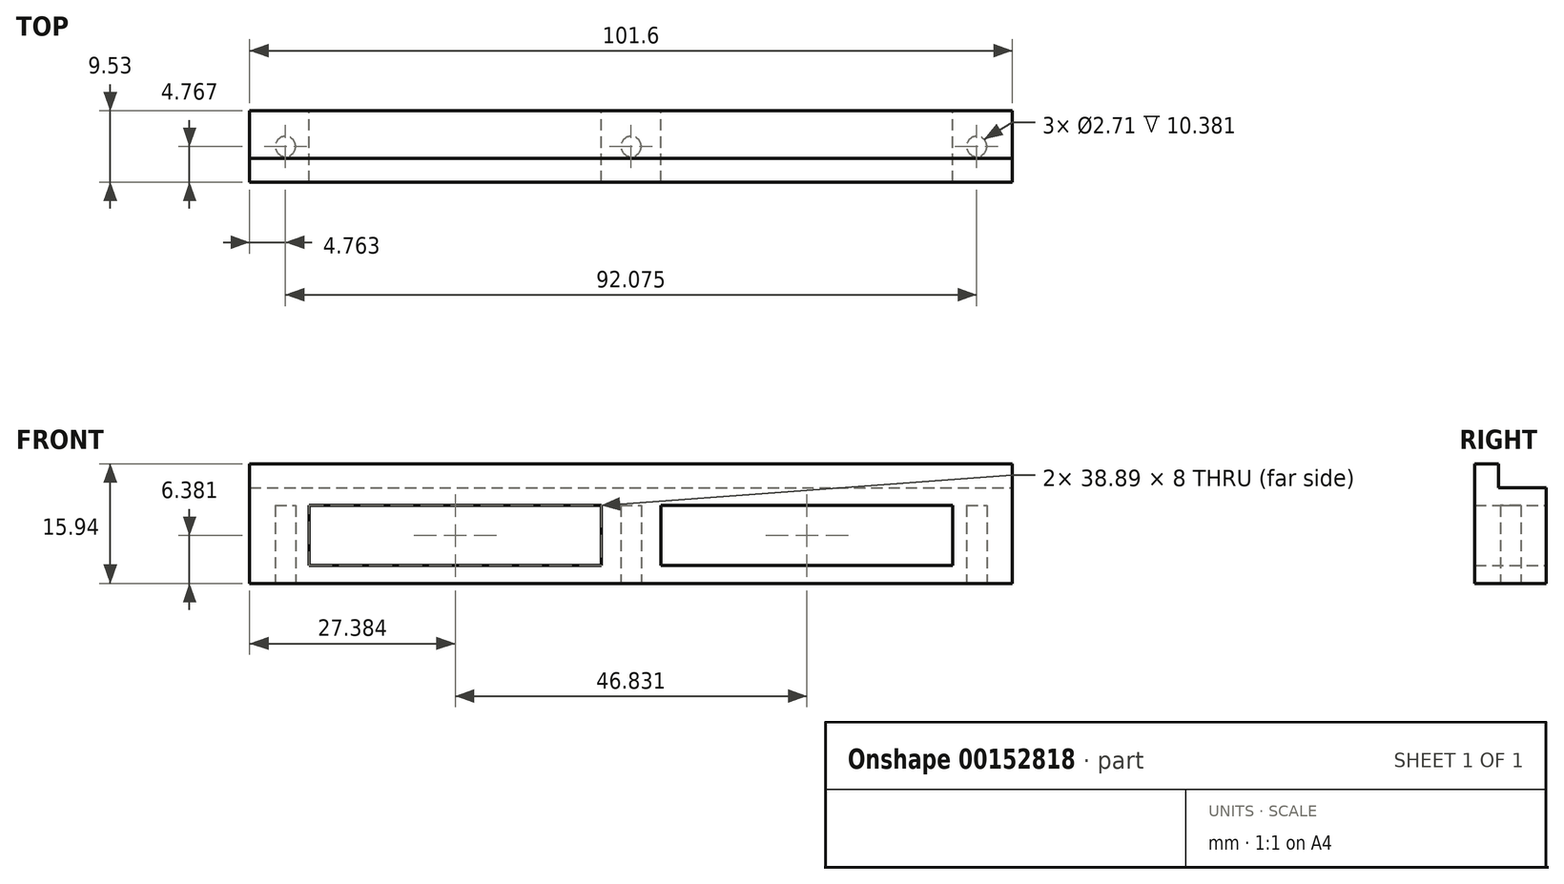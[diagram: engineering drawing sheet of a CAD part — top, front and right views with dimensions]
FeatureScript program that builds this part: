
annotation { "Feature Type Name" : "Feature", "Feature Type Description" : "" }
export const myFeature = defineFeature(function(context is Context, id is Id, definition is map)
    precondition{}
    {
        {
            var Q0;
            Q0=qCreatedBy(makeId("Top.planeOp"),FACE);
            var sketch = newSketch(context, id + "F0", { "sketchPlane" : qUnion([Q0])});
            skLineSegment(sketch, "E0.bottom", {"start": v(0, 0) * mm, "end": v(101.6, 0) * mm});
            skLineSegment(sketch, "E0.top", {"start": v(0, -9.53) * mm, "end": v(101.6, -9.53) * mm});
            skLineSegment(sketch, "E0.left", {"start": v(0, 0) * mm, "end": v(0, -9.53) * mm});
            skLineSegment(sketch, "E0.right", {"start": v(101.6, 0) * mm, "end": v(101.6, -9.52) * mm});
            skSolve(sketch);
        }
        {
            var Q0;
            Q0 = qSketchRegion(id + "F0", true);
            extrude(context, id + "F1", {"entities" : qUnion([Q0]), "depth" : 12.76 * mm});
        }
        {
            var Q0;
            Q0=makeQuery(id+"F1.opExtrude","CAP_FACE",FACE,{"disambiguationData":[OSD([sQuery(id+"F0.wireOp",EDGE,"E0.bottom"),sQuery(id+"F0.wireOp",EDGE,"E0.top"),sQuery(id+"F0.wireOp",EDGE,"E0.left"),sQuery(id+"F0.wireOp",EDGE,"E0.right")])],"isStart":false});
            var sketch = newSketch(context, id + "F2", { "sketchPlane" : qUnion([Q0])});
            skLineSegment(sketch, "E1.bottom", {"start": v(0, -9.53) * mm, "end": v(101.6, -9.53) * mm});
            skLineSegment(sketch, "E1.top", {"start": v(0, -6.35) * mm, "end": v(101.6, -6.35) * mm});
            skLineSegment(sketch, "E1.left", {"start": v(0, -9.53) * mm, "end": v(0, -6.35) * mm});
            skLineSegment(sketch, "E1.right", {"start": v(101.6, -9.53) * mm, "end": v(101.6, -6.35) * mm});
            skSolve(sketch);
        }
        {
            var Q0;
            Q0 = qSketchRegion(id + "F2", true);
            extrude(context, id + "F3", {"entities" : qUnion([Q0]), "operationType" : NewBodyOperationType.ADD, "depth" : 3.17 * mm});
        }
        {
            var Q0;
            Q0=makeQuery(id+"F1.opExtrude","SWEPT_FACE",FACE,{"disambiguationData":[OSD([sQuery(id+"F0.wireOp",EDGE,"E0.bottom")])]});
            var sketch = newSketch(context, id + "F4", { "sketchPlane" : qUnion([Q0])});
            skLineSegment(sketch, "E2.bottom", {"start": v(-93.66, 10.38) * mm, "end": v(-54.77, 10.38) * mm});
            skLineSegment(sketch, "E2.top", {"start": v(-93.66, 2.38) * mm, "end": v(-54.77, 2.38) * mm});
            skLineSegment(sketch, "E2.left", {"start": v(-93.66, 10.38) * mm, "end": v(-93.66, 2.38) * mm});
            skLineSegment(sketch, "E2.right", {"start": v(-54.77, 10.38) * mm, "end": v(-54.77, 2.38) * mm});
            skLineSegment(sketch, "E3.bottom", {"start": v(-46.83, 10.38) * mm, "end": v(-7.94, 10.38) * mm});
            skLineSegment(sketch, "E3.top", {"start": v(-46.83, 2.38) * mm, "end": v(-7.94, 2.38) * mm});
            skLineSegment(sketch, "E3.left", {"start": v(-46.83, 10.38) * mm, "end": v(-46.83, 2.38) * mm});
            skLineSegment(sketch, "E3.right", {"start": v(-7.94, 10.38) * mm, "end": v(-7.94, 2.38) * mm});
            skLineSegment(sketch, "E4", {"start": v(0, 6.38) * mm, "end": v(-7.94, 6.38) * mm, "construction": true});
            skLineSegment(sketch, "E5", {"start": v(-27.38, 2.38) * mm, "end": v(-27.38, 0) * mm, "construction": true});
            skLineSegment(sketch, "E6", {"start": v(-46.83, 6.38) * mm, "end": v(-54.77, 6.38) * mm, "construction": true});
            skLineSegment(sketch, "E7", {"start": v(-93.66, 6.38) * mm, "end": v(-101.6, 6.38) * mm, "construction": true});
            skSolve(sketch);
        }
        {
            var Q0;
            Q0 = qSketchRegion(id + "F4", true);
            var Q1;
            Q1=makeQuery(id+"F3.boolean.opBoolean","MERGE",FACE,{"derivedFrom":[makeQuery(id+"F1.opExtrude","SWEPT_FACE",FACE,{"disambiguationData":[OSD([sQuery(id+"F0.wireOp",EDGE,"E0.top")])]}),makeQuery(id+"F3.opExtrude","SWEPT_FACE",FACE,{"disambiguationData":[OSD([sQuery(id+"F2.wireOp",EDGE,"E1.bottom")])]})]});
            extrude(context, id + "F5", {"entities" : qUnion([Q0]), "operationType" : NewBodyOperationType.REMOVE, "endBound" : BoundingType.UP_TO_SURFACE, "oppositeDirection" : true, "endBoundEntityFace" : qUnion([Q1]), "depth" : 25.4 * mm});
        }
        {
            var Q0;
            Q0=makeQuery(id+"F1.opExtrude","CAP_FACE",FACE,{"disambiguationData":[OSD([sQuery(id+"F0.wireOp",EDGE,"E0.bottom"),sQuery(id+"F0.wireOp",EDGE,"E0.top"),sQuery(id+"F0.wireOp",EDGE,"E0.left"),sQuery(id+"F0.wireOp",EDGE,"E0.right")])],"isStart":true});
            var sketch = newSketch(context, id + "F6", { "sketchPlane" : qUnion([Q0])});
            skLineSegment(sketch, "E8.bottom", {"start": v(101.6, 4.76) * mm, "end": v(96.84, 4.76) * mm, "construction": true});
            skLineSegment(sketch, "E8.top", {"start": v(101.6, 9.53) * mm, "end": v(96.84, 9.53) * mm, "construction": true});
            skLineSegment(sketch, "E8.left", {"start": v(101.6, 4.76) * mm, "end": v(101.6, 9.53) * mm, "construction": true});
            skLineSegment(sketch, "E8.right", {"start": v(96.84, 4.76) * mm, "end": v(96.84, 9.53) * mm, "construction": true});
            skLineSegment(sketch, "E9.bottom", {"start": v(0, 4.76) * mm, "end": v(4.76, 4.76) * mm, "construction": true});
            skLineSegment(sketch, "E9.top", {"start": v(0, 9.53) * mm, "end": v(4.76, 9.53) * mm, "construction": true});
            skLineSegment(sketch, "E9.left", {"start": v(0, 4.76) * mm, "end": v(0, 9.53) * mm, "construction": true});
            skLineSegment(sketch, "E9.right", {"start": v(4.76, 4.76) * mm, "end": v(4.76, 9.53) * mm, "construction": true});
            skLineSegment(sketch, "E10", {"start": v(50.8, 0) * mm, "end": v(50.8, 9.53) * mm, "construction": true});
            skCircle(sketch, "E11", {"center": v(96.84, 4.76) * mm, "radius": 1.35 * mm});
            skCircle(sketch, "E12", {"center": v(50.8, 4.76) * mm, "radius": 1.35 * mm});
            skCircle(sketch, "E13", {"center": v(4.76, 4.76) * mm, "radius": 1.35 * mm});
            skSolve(sketch);
        }
        {
            var Q0;
            Q0 = qSketchRegion(id + "F6", true);
            var Q1;
            Q1=makeQuery(id+"F5.boolean.opBoolean","COPY",FACE,{"derivedFrom":makeQuery(id+"F5.opExtrude","SWEPT_FACE",FACE,{"disambiguationData":[OSD([sQuery(id+"F4.wireOp",EDGE,"E2.bottom")])]})});
            extrude(context, id + "F7", {"entities" : qUnion([Q0]), "operationType" : NewBodyOperationType.REMOVE, "endBound" : BoundingType.UP_TO_SURFACE, "oppositeDirection" : true, "endBoundEntityFace" : qUnion([Q1]), "depth" : 25.4 * mm});
        }
    });
